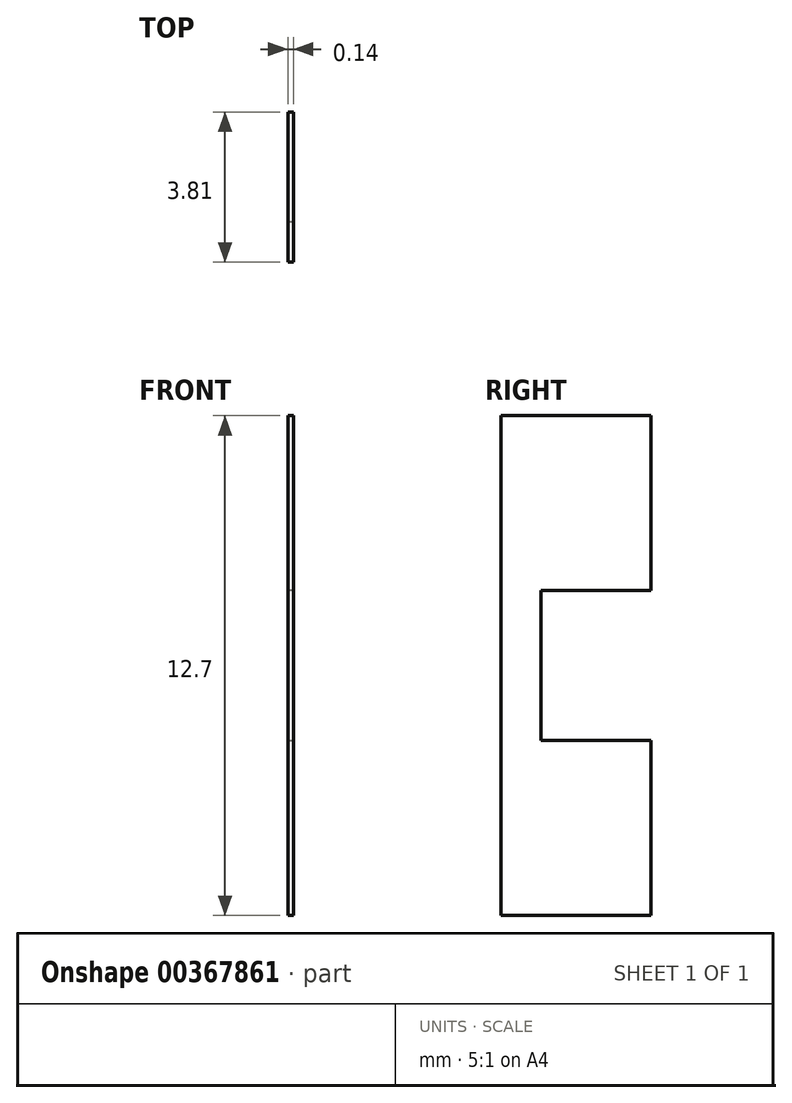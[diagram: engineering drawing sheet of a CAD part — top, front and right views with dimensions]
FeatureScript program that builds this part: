
annotation { "Feature Type Name" : "Feature", "Feature Type Description" : "" }
export const myFeature = defineFeature(function(context is Context, id is Id, definition is map)
    precondition{}
    {
        {
            var Q0;
            Q0=qCreatedBy(makeId("Right.planeOp"),FACE);
            var sketch = newSketch(context, id + "F0", { "sketchPlane" : qUnion([Q0])});
            skLineSegment(sketch, "E0", {"start": v(-8, 0) * mm, "end": v(-8, 37.52) * mm});
            skLineSegment(sketch, "E1", {"start": v(-8, 37.52) * mm, "end": v(-18.17, 37.52) * mm});
            skLineSegment(sketch, "E2", {"start": v(-18.17, 37.52) * mm, "end": v(-18.17, 32.7) * mm});
            skLineSegment(sketch, "E3", {"start": v(-18.17, 32.7) * mm, "end": v(-21.98, 32.7) * mm});
            skLineSegment(sketch, "E4", {"start": v(-21.98, 32.7) * mm, "end": v(-21.98, 34.98) * mm});
            skLineSegment(sketch, "E5", {"start": v(-15.63, 41.33) * mm, "end": v(-10.55, 41.33) * mm});
            skLineSegment(sketch, "E6", {"start": v(-4.2, 34.98) * mm, "end": v(-4.2, 0) * mm});
            skPoint(sketch, "E7.visualSharp", {"position": v(-21.98, 41.33) * mm});
            skArc(sketch, "E7.filletArc", {"start": v(-15.63, 41.33) * mm, "mid": v(-20.12, 39.47) * mm, "end": v(-21.98, 34.98) * mm});
            skPoint(sketch, "E8.visualSharp", {"position": v(-4.2, 41.33) * mm});
            skArc(sketch, "E8.filletArc", {"start": v(-4.2, 34.98) * mm, "mid": v(-6.06, 39.47) * mm, "end": v(-10.55, 41.33) * mm});
            skLineSegment(sketch, "E9.MirrorCS", {"start": v(-18.17, -37.52) * mm, "end": v(-18.17, -32.7) * mm});
            skLineSegment(sketch, "E10.MirrorCS", {"start": v(-21.98, -32.7) * mm, "end": v(-21.98, -34.98) * mm});
            skLineSegment(sketch, "E11.MirrorCS", {"start": v(-8, -37.52) * mm, "end": v(-18.17, -37.52) * mm});
            skPoint(sketch, "E12.MirrorP", {"position": v(-4.2, -41.33) * mm});
            skArc(sketch, "E13.MirrorCS", {"start": v(-15.63, -41.33) * mm, "mid": v(-20.12, -39.47) * mm, "end": v(-21.98, -34.98) * mm});
            skLineSegment(sketch, "E14.MirrorCS", {"start": v(-18.17, -32.7) * mm, "end": v(-21.98, -32.7) * mm});
            skArc(sketch, "E15.MirrorCS", {"start": v(-4.2, -34.98) * mm, "mid": v(-6.06, -39.47) * mm, "end": v(-10.55, -41.33) * mm});
            skPoint(sketch, "E16.MirrorP", {"position": v(-21.98, -41.33) * mm});
            skLineSegment(sketch, "E17.MirrorCS", {"start": v(-15.63, -41.33) * mm, "end": v(-10.55, -41.33) * mm});
            skLineSegment(sketch, "E18.MirrorCS", {"start": v(-8, 0) * mm, "end": v(-8, -37.52) * mm});
            skLineSegment(sketch, "E19.MirrorCS", {"start": v(-4.2, -34.98) * mm, "end": v(-4.2, 0) * mm});
            skSolve(sketch);
        }
        {
            var Q0;
            Q0=makeQuery(id+"F0.imprint","IMPRINT",FACE,{"disambiguationData":[TD([[makeQuery(id+"F0.imprint","IMPRINT",EDGE,{"derivedFrom":sQuery(id+"F0.wireOp",EDGE,"E0")}),-1.0]])]});
            extrude(context, id + "F1", {"entities" : qUnion([Q0]), "depth" : 3.44 / 50.8 * mm, "hasSecondDirection" : true, "secondDirectionOppositeDirection" : true, "secondDirectionDepth" : 3.44 / 50.8 * mm});
        }
        {
            var Q0;
            Q0=makeQuery(id+"F1.opExtrude","SWEPT_FACE",FACE,{"disambiguationData":[OSD([sQuery(id+"F0.wireOp",EDGE,"E6"),sQuery(id+"F0.wireOp",EDGE,"E19.MirrorCS")])]});
            var sketch = newSketch(context, id + "F2", { "sketchPlane" : qUnion([Q0])});
            skCircle(sketch, "E20", {"center": v(0, 0) * mm, "radius": 1.9 * mm});
            skSolve(sketch);
        }
        {
            var Q0;
            Q0=makeQuery(id+"F2.imprint","IMPRINT",FACE,{"disambiguationData":[TD([[makeQuery(id+"F2.imprint","IMPRINT",EDGE,{"derivedFrom":sQuery(id+"F2.wireOp",EDGE,"E20")}),1.0]])]});
            extrude(context, id + "F3", {"entities" : qUnion([Q0]), "operationType" : NewBodyOperationType.REMOVE, "oppositeDirection" : true, "depth" : 2.8 * mm});
        }
        {
            var Q0;
            Q0=makeQuery(id+"F1.opExtrude","SWEPT_FACE",FACE,{"disambiguationData":[OSD([sQuery(id+"F0.wireOp",EDGE,"E6"),sQuery(id+"F0.wireOp",EDGE,"E19.MirrorCS")])]});
            var sketch = newSketch(context, id + "F4", { "sketchPlane" : qUnion([Q0])});
            skLineSegment(sketch, "E21.bottom", {"start": v(22.03, 6.35) * mm, "end": v(-22.03, 6.35) * mm});
            skLineSegment(sketch, "E21.top", {"start": v(30.92, 50.72) * mm, "end": v(-30.92, 50.72) * mm});
            skLineSegment(sketch, "E21.left", {"start": v(30.92, 15.24) * mm, "end": v(30.92, 50.72) * mm});
            skLineSegment(sketch, "E21.right", {"start": v(-30.92, 15.24) * mm, "end": v(-30.92, 50.72) * mm});
            skLineSegment(sketch, "E22.MirrorCS", {"start": v(22.03, -6.35) * mm, "end": v(-22.03, -6.35) * mm});
            skLineSegment(sketch, "E23.MirrorCS", {"start": v(-30.92, -15.24) * mm, "end": v(-30.92, -50.72) * mm});
            skLineSegment(sketch, "E24.MirrorCS", {"start": v(30.92, -15.24) * mm, "end": v(30.92, -50.72) * mm});
            skLineSegment(sketch, "E25.MirrorCS", {"start": v(30.92, -50.72) * mm, "end": v(-30.92, -50.72) * mm});
            skPoint(sketch, "E26.visualSharp", {"position": v(-30.92, 6.35) * mm});
            skArc(sketch, "E26.filletArc", {"start": v(-30.92, 15.24) * mm, "mid": v(-28.32, 8.95) * mm, "end": v(-22.03, 6.35) * mm});
            skPoint(sketch, "E27.visualSharp", {"position": v(-30.92, -6.35) * mm});
            skArc(sketch, "E27.filletArc", {"start": v(-22.03, -6.35) * mm, "mid": v(-28.32, -8.95) * mm, "end": v(-30.92, -15.24) * mm});
            skPoint(sketch, "E28.visualSharp", {"position": v(30.92, 6.35) * mm});
            skArc(sketch, "E28.filletArc", {"start": v(22.03, 6.35) * mm, "mid": v(28.32, 8.95) * mm, "end": v(30.92, 15.24) * mm});
            skPoint(sketch, "E29.visualSharp", {"position": v(30.92, -6.35) * mm});
            skArc(sketch, "E29.filletArc", {"start": v(30.92, -15.24) * mm, "mid": v(28.32, -8.95) * mm, "end": v(22.03, -6.35) * mm});
            skSolve(sketch);
        }
        {
            var Q0;
            Q0 = qSketchRegion(id + "F4", true);
            extrude(context, id + "F5", {"entities" : qUnion([Q0]), "operationType" : NewBodyOperationType.REMOVE, "oppositeDirection" : true, "depth" : 25.4 * mm});
        }
    });
